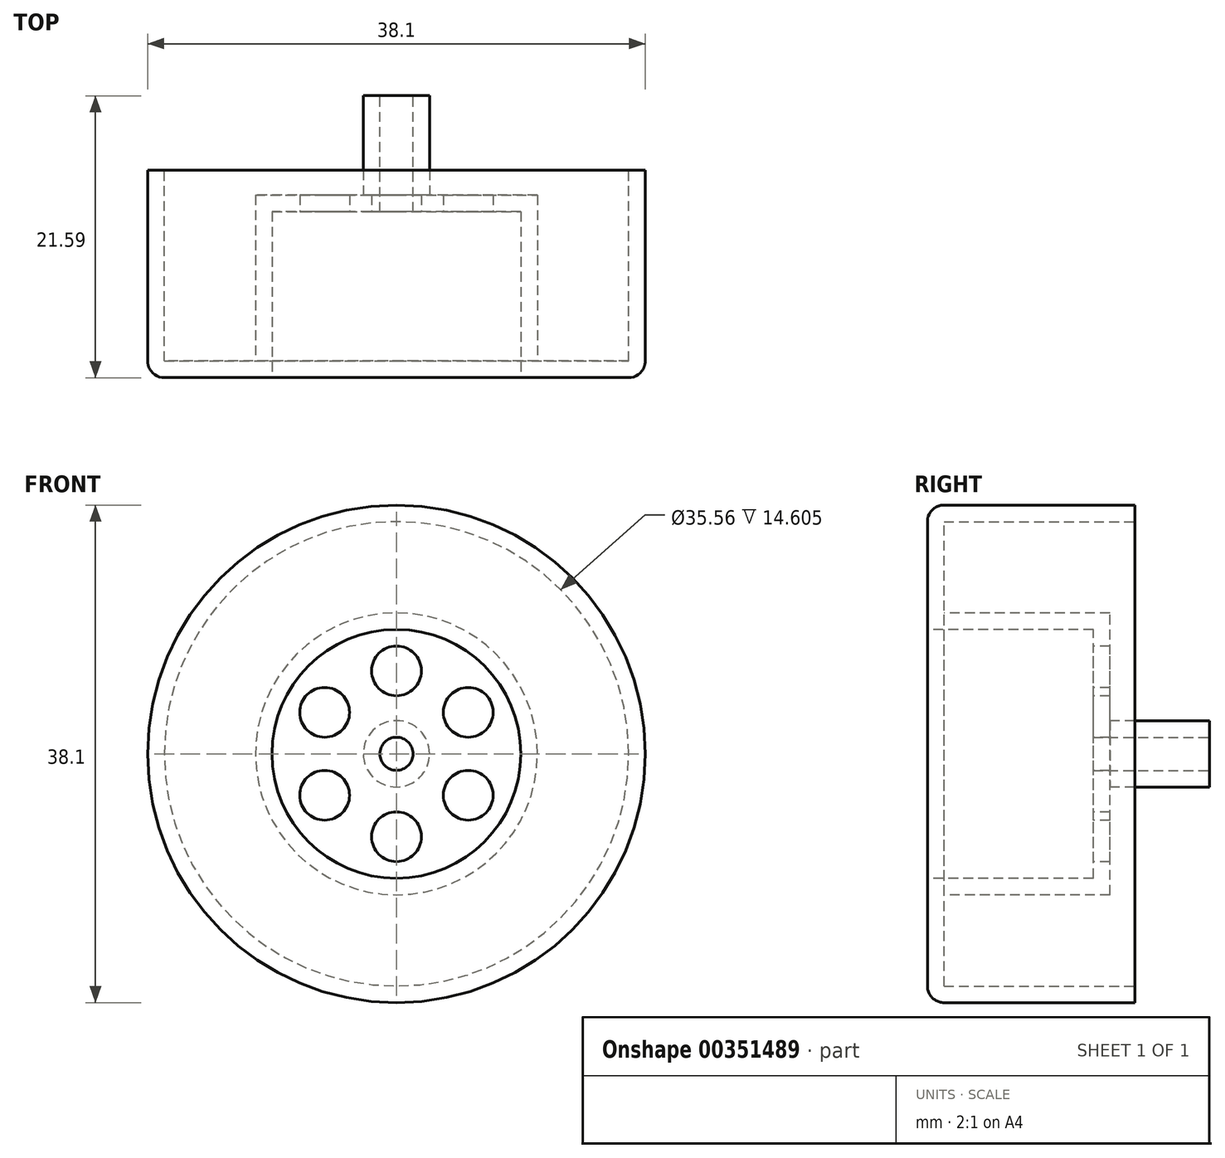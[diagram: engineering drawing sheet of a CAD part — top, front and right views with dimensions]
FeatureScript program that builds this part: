
annotation { "Feature Type Name" : "Feature", "Feature Type Description" : "" }
export const myFeature = defineFeature(function(context is Context, id is Id, definition is map)
    precondition{}
    {
        {
            var Q0;
            Q0=qCreatedBy(makeId("Front.planeOp"),FACE);
            var sketch = newSketch(context, id + "F0", { "sketchPlane" : qUnion([Q0])});
            skCircle(sketch, "E0", {"center": v(0, 0) * mm, "radius": 19.05 * mm});
            skSolve(sketch);
        }
        {
            var Q0;
            Q0 = qSketchRegion(id + "F0", true);
            extrude(context, id + "F1", {"entities" : qUnion([Q0]), "depth" : 15.88 * mm, "symmetric" : true});
        }
        {
            var Q0;
            Q0=makeQuery(id+"F1.opExtrude","CAP_FACE",FACE,{"disambiguationData":[OSD([sQuery(id+"F0.wireOp",EDGE,"E0")])],"isStart":false});
            var sketch = newSketch(context, id + "F2", { "sketchPlane" : qUnion([Q0])});
            skCircle(sketch, "E1", {"center": v(0, 0) * mm, "radius": 9.53 * mm});
            skSolve(sketch);
        }
        {
            var Q0;
            Q0 = qSketchRegion(id + "F2", true);
            extrude(context, id + "F3", {"entities" : qUnion([Q0]), "operationType" : NewBodyOperationType.REMOVE, "oppositeDirection" : true, "depth" : 12.7 * mm});
        }
        {
            var Q0;
            Q0=makeQuery(id+"F1.opExtrude","CAP_FACE",FACE,{"disambiguationData":[OSD([sQuery(id+"F0.wireOp",EDGE,"E0")])],"isStart":true});
            var Q1;
            Q1=makeQuery(id+"F1.opExtrude","SWEPT_BODY",BODY,{"disambiguationData":[OSD([sQuery(id+"F0.wireOp",EDGE,"E0")])]});
            shell(context, id + "F4", {"entities" : qUnion([Q0]), "parts" : qUnion([Q1]), "thickness" : 1.27 * mm});
        }
        {
            var Q0;
            Q0=makeQuery(id+"F3.boolean.opBoolean","COPY",FACE,{"derivedFrom":makeQuery(id+"F3.opExtrude","CAP_FACE",FACE,{"disambiguationData":[OSD([sQuery(id+"F2.wireOp",EDGE,"E1")])],"isStart":false})});
            var sketch = newSketch(context, id + "F5", { "sketchPlane" : qUnion([Q0])});
            skCircle(sketch, "E2", {"center": v(0, 6.35) * mm, "radius": 1.9 * mm});
            skCircle(sketch, "E3.1.0", {"center": v(-5.5, 3.17) * mm, "radius": 1.9 * mm});
            skCircle(sketch, "E3.2.0", {"center": v(-5.5, -3.18) * mm, "radius": 1.9 * mm});
            skPoint(sketch, "E3.center", {"position": v(0, 0) * mm});
            skLineSegment(sketch, "E3.anchor1", {"start": v(0, 0) * mm, "end": v(0, 6.35) * mm, "construction": true});
            skLineSegment(sketch, "E3.anchor2", {"start": v(0, 0) * mm, "end": v(5.5, 3.18) * mm, "construction": true});
            skCircle(sketch, "E4.1.3.0", {"center": v(0, -6.35) * mm, "radius": 1.9 * mm});
            skCircle(sketch, "E4.1.4.0", {"center": v(5.5, -3.17) * mm, "radius": 1.9 * mm});
            skCircle(sketch, "E4.1.5.0", {"center": v(5.5, 3.18) * mm, "radius": 1.9 * mm});
            skSolve(sketch);
        }
        {
            var Q0;
            Q0 = qSketchRegion(id + "F5", true);
            extrude(context, id + "F6", {"entities" : qUnion([Q0]), "operationType" : NewBodyOperationType.REMOVE, "endBound" : BoundingType.THROUGH_ALL, "oppositeDirection" : true, "depth" : 25.4 * mm});
        }
        {
            var Q0;
            {var subQ0=sQuery(id+"F2.wireOp",EDGE,"E1");Q0=makeQuery(id+"F4.opShell","OFFSET_FACE",FACE,{"disambiguationData":[OSD([subQ0]),TDD([makeQuery(id+"F3.boolean.opBoolean","COPY",FACE,{"derivedFrom":makeQuery(id+"F3.opExtrude","CAP_FACE",FACE,{"disambiguationData":[OSD([subQ0])],"isStart":false})})])]});}
            var sketch = newSketch(context, id + "F7", { "sketchPlane" : qUnion([Q0])});
            skCircle(sketch, "E5", {"center": v(0, 0) * mm, "radius": 2.54 * mm});
            skSolve(sketch);
        }
        {
            var Q0;
            Q0 = qSketchRegion(id + "F7", true);
            extrude(context, id + "F8", {"entities" : qUnion([Q0]), "operationType" : NewBodyOperationType.ADD, "depth" : 7.62 * mm});
        }
        {
            var Q0;
            Q0=makeQuery(id+"F8.opExtrude","CAP_FACE",FACE,{"disambiguationData":[OSD([sQuery(id+"F7.wireOp",EDGE,"E5")])],"isStart":false});
            var sketch = newSketch(context, id + "F9", { "sketchPlane" : qUnion([Q0])});
            skCircle(sketch, "E6", {"center": v(0, 0) * mm, "radius": 1.27 * mm});
            skSolve(sketch);
        }
        {
            var Q0;
            Q0=makeQuery(id+"F9.imprint","IMPRINT",FACE,{"disambiguationData":[TD([[makeQuery(id+"F9.imprint","IMPRINT",EDGE,{"derivedFrom":sQuery(id+"F9.wireOp",EDGE,"E6")}),1.0]])]});
            extrude(context, id + "F10", {"entities" : qUnion([Q0]), "operationType" : NewBodyOperationType.REMOVE, "endBound" : BoundingType.THROUGH_ALL, "oppositeDirection" : true, "depth" : 25.4 * mm});
        }
        {
            var Q0;
            Q0=makeQuery(id+"F1.opExtrude","CAP_EDGE",EDGE,{"disambiguationData":[OSD([sQuery(id+"F0.wireOp",EDGE,"E0")])],"isStart":false});
            var Q1;
            Q1=makeQuery(id+"F3.boolean.opBoolean","COPY",EDGE,{"derivedFrom":makeQuery(id+"F3.opExtrude","CAP_EDGE",EDGE,{"disambiguationData":[OSD([sQuery(id+"F2.wireOp",EDGE,"E1")])],"isStart":true})});
            fillet(context, id + "F11", {"entities" : qUnion([Q0, Q1]), "radius" : 1.27 * mm, "tangentPropagation" : true, "allowEdgeOverflow" : false});
        }
    });
